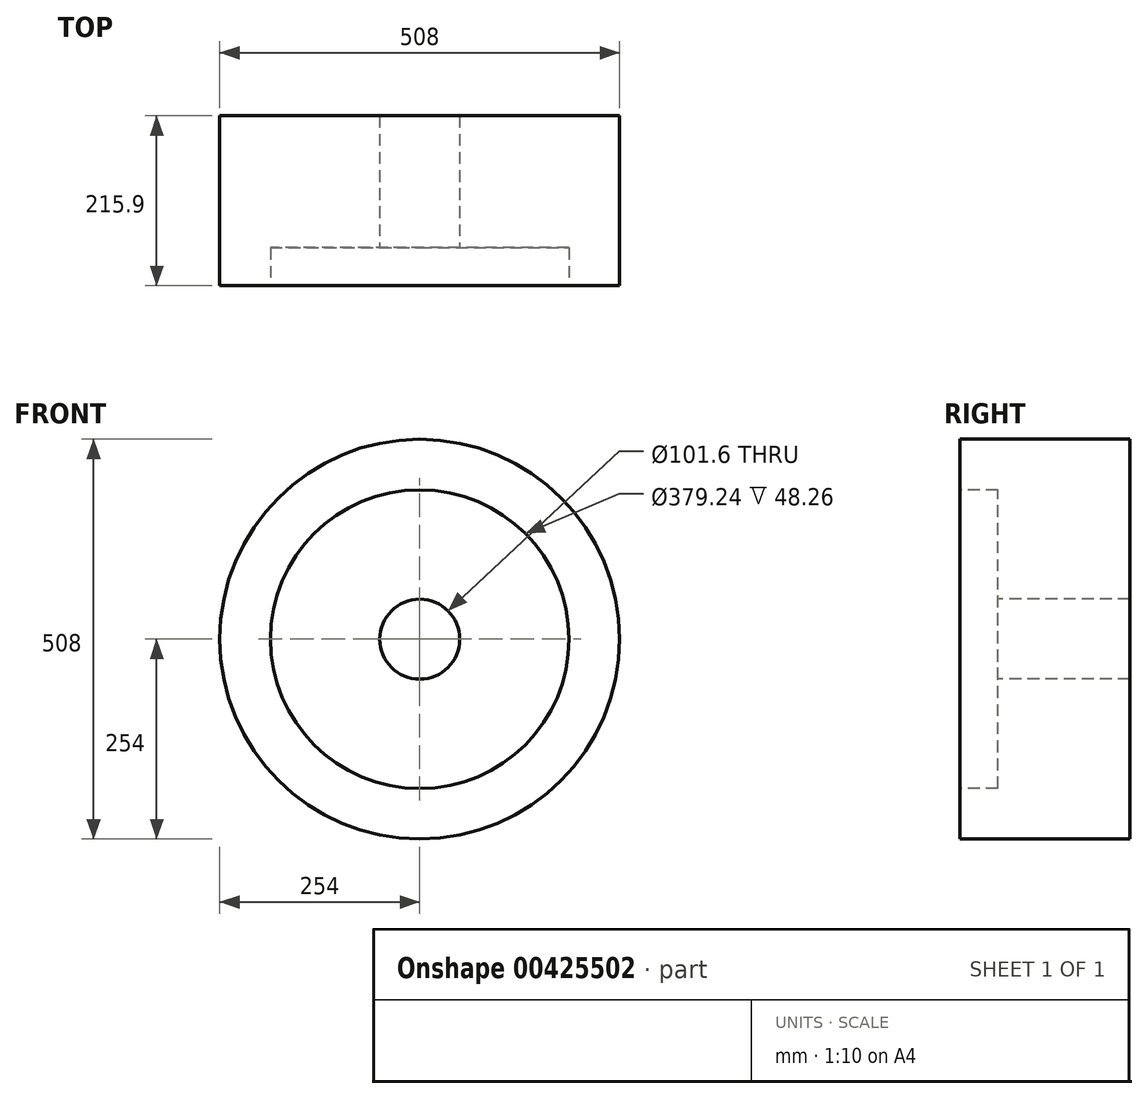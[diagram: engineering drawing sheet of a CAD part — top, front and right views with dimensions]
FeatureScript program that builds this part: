
annotation { "Feature Type Name" : "Feature", "Feature Type Description" : "" }
export const myFeature = defineFeature(function(context is Context, id is Id, definition is map)
    precondition{}
    {
        {
            var Q0;
            Q0=qCreatedBy(makeId("Front.planeOp"),FACE);
            var sketch = newSketch(context, id + "F0", { "sketchPlane" : qUnion([Q0])});
            skCircle(sketch, "E0", {"center": v(0, 0) * mm, "radius": 254 * mm});
            skSolve(sketch);
        }
        {
            var Q0;
            Q0=makeQuery(id+"F0.imprint","IMPRINT",FACE,{"disambiguationData":[TD([[makeQuery(id+"F0.imprint","IMPRINT",EDGE,{"derivedFrom":sQuery(id+"F0.wireOp",EDGE,"E0")}),1.0]])]});
            extrude(context, id + "F1", {"entities" : qUnion([Q0]), "depth" : 215.9 * mm});
        }
        {
            var Q0;
            Q0=makeQuery(id+"F1.opExtrude","CAP_FACE",FACE,{"disambiguationData":[OSD([sQuery(id+"F0.wireOp",EDGE,"E0")])],"isStart":false});
            var sketch = newSketch(context, id + "F2", { "sketchPlane" : qUnion([Q0])});
            skCircle(sketch, "E1", {"center": v(0, 0) * mm, "radius": 50.8 * mm});
            skSolve(sketch);
        }
        {
            var Q0;
            Q0=makeQuery(id+"F2.imprint","IMPRINT",FACE,{"disambiguationData":[TD([[makeQuery(id+"F2.imprint","IMPRINT",EDGE,{"derivedFrom":sQuery(id+"F2.wireOp",EDGE,"E1")}),1.0]])]});
            extrude(context, id + "F3", {"entities" : qUnion([Q0]), "operationType" : NewBodyOperationType.REMOVE, "endBound" : BoundingType.THROUGH_ALL, "oppositeDirection" : true, "depth" : 25.4 * mm});
        }
        {
            var Q0;
            Q0=makeQuery(id+"F1.opExtrude","CAP_FACE",FACE,{"disambiguationData":[OSD([sQuery(id+"F0.wireOp",EDGE,"E0")])],"isStart":false});
            var sketch = newSketch(context, id + "F4", { "sketchPlane" : qUnion([Q0])});
            skCircle(sketch, "E2", {"center": v(0, 0) * mm, "radius": 189.62 * mm});
            skSolve(sketch);
        }
        {
            var Q0;
            Q0=makeQuery(id+"F4.imprint","IMPRINT",FACE,{"disambiguationData":[TD([[makeQuery(id+"F4.imprint","IMPRINT",EDGE,{"derivedFrom":sQuery(id+"F4.wireOp",EDGE,"E2")}),1.0]])]});
            extrude(context, id + "F5", {"entities" : qUnion([Q0]), "operationType" : NewBodyOperationType.REMOVE, "oppositeDirection" : true, "depth" : 48.26 * mm});
        }
    });
